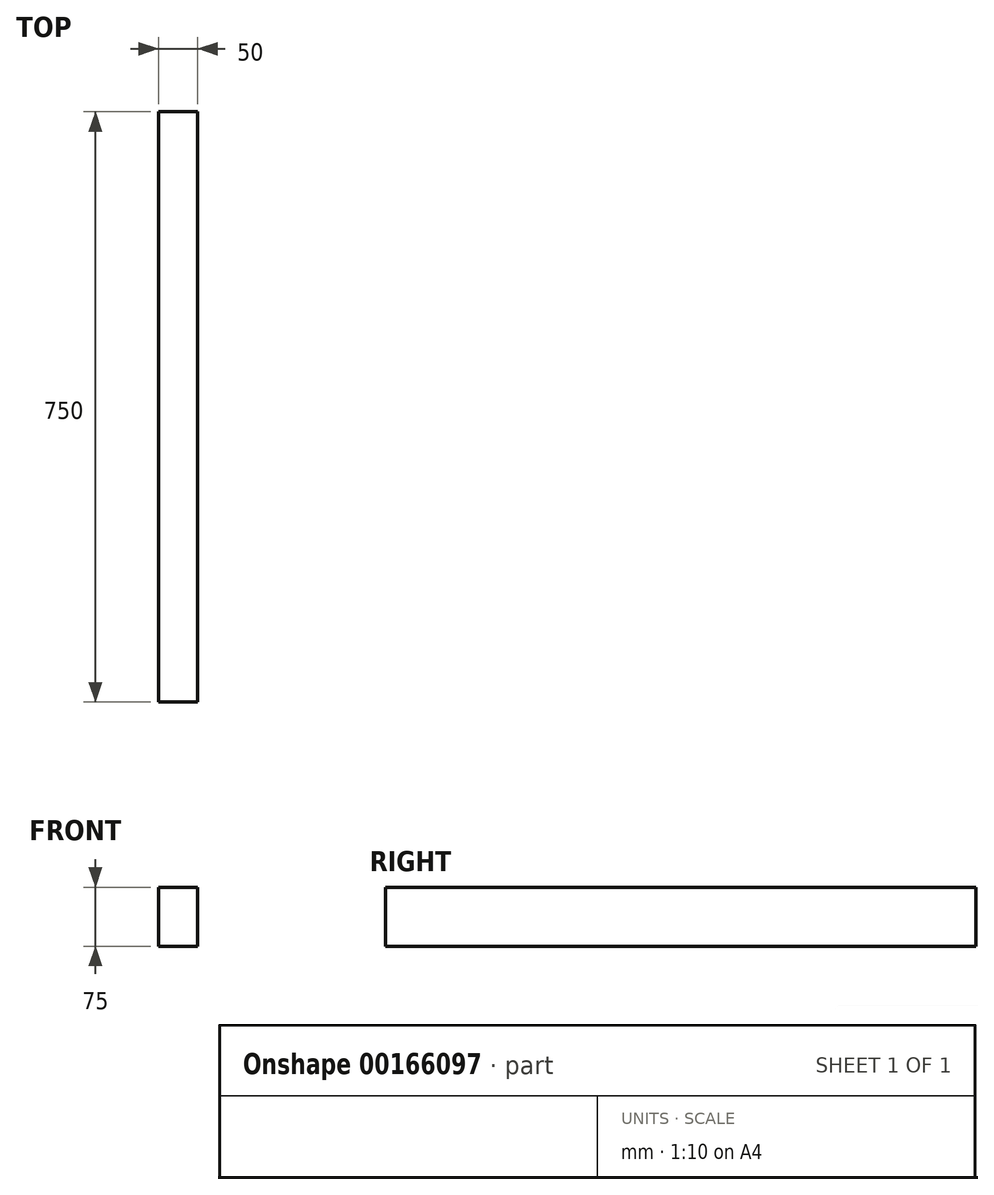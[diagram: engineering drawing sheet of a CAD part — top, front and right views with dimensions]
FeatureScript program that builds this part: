
annotation { "Feature Type Name" : "Feature", "Feature Type Description" : "" }
export const myFeature = defineFeature(function(context is Context, id is Id, definition is map)
    precondition{}
    {
        {
            var Q0;
            Q0=qCreatedBy(makeId("Front.planeOp"),FACE);
            var sketch = newSketch(context, id + "F0", { "sketchPlane" : qUnion([Q0])});
            skLineSegment(sketch, "E0.bottom", {"start": v(25, 37.5) * mm, "end": v(-25, 37.5) * mm});
            skLineSegment(sketch, "E0.top", {"start": v(25, -37.5) * mm, "end": v(-25, -37.5) * mm});
            skLineSegment(sketch, "E0.left", {"start": v(25, 37.5) * mm, "end": v(25, -37.5) * mm});
            skLineSegment(sketch, "E0.right", {"start": v(-25, 37.5) * mm, "end": v(-25, -37.5) * mm});
            skPoint(sketch, "E0.middle", {"position": v(0, 0) * mm});
            skSolve(sketch);
        }
        {
            var Q0;
            Q0 = qSketchRegion(id + "F0", true);
            extrude(context, id + "F1", {"entities" : qUnion([Q0]), "depth" : 750 * mm});
        }
    });
